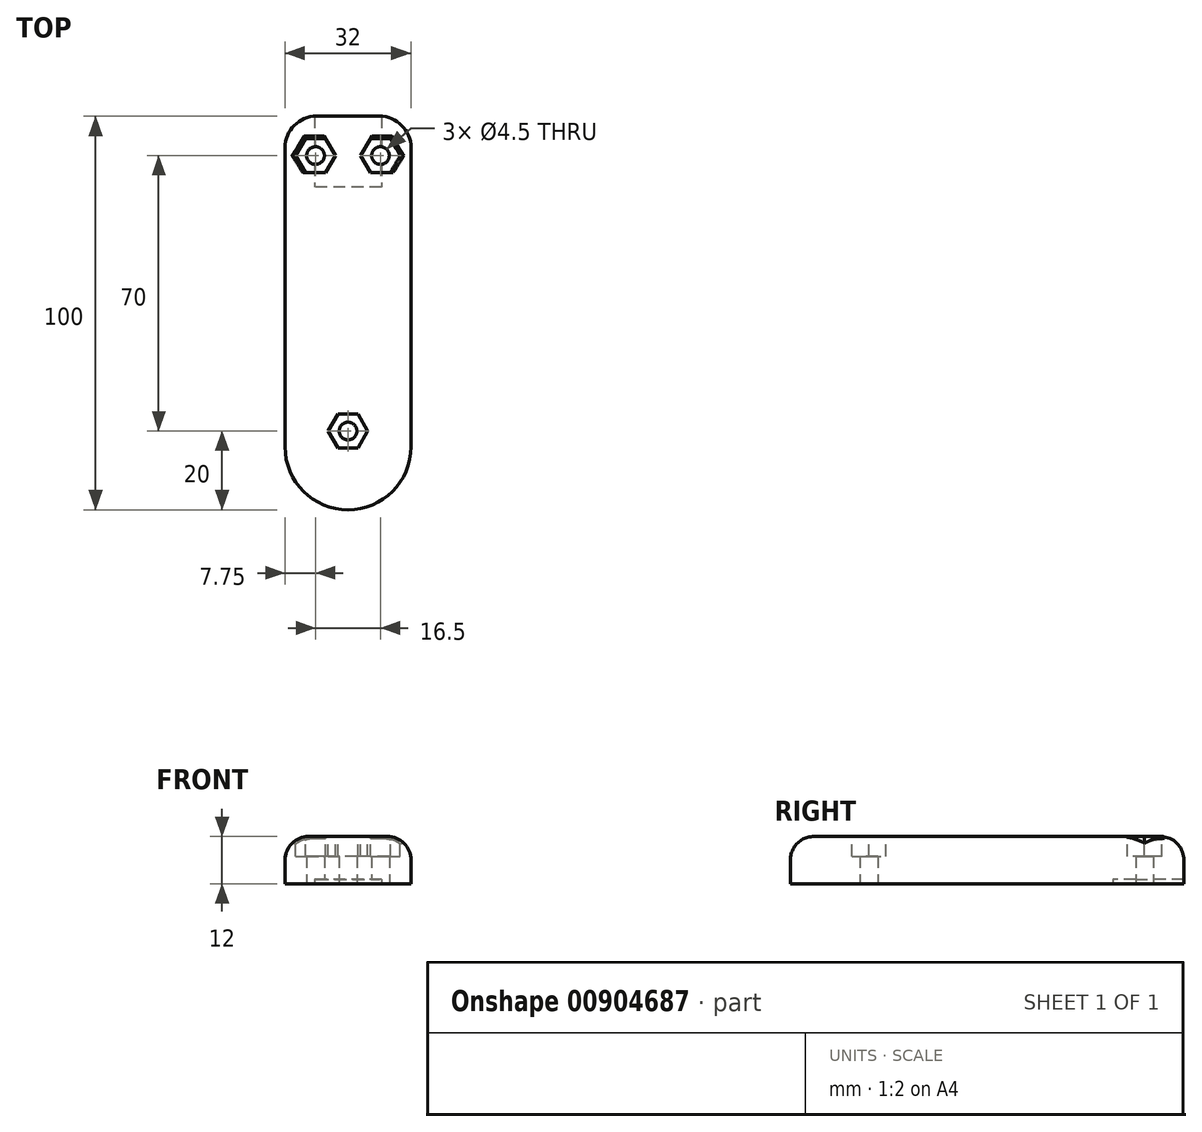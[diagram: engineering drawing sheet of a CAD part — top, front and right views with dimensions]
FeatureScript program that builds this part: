
annotation { "Feature Type Name" : "Feature", "Feature Type Description" : "" }
export const myFeature = defineFeature(function(context is Context, id is Id, definition is map)
    precondition{}
    {
        {
            var Q0;
            Q0=qCreatedBy(makeId("Top.planeOp"),FACE);
            var sketch = newSketch(context, id + "F0", { "sketchPlane" : qUnion([Q0])});
            skCircle(sketch, "E0", {"center": v(-8.25, -10) * mm, "radius": 2.25 * mm});
            skLineSegment(sketch, "E1", {"start": v(0, 0) * mm, "end": v(-8, 0) * mm});
            skLineSegment(sketch, "E2", {"start": v(-16, -8) * mm, "end": v(-16, -84) * mm});
            skLineSegment(sketch, "E3", {"start": v(0, -100) * mm, "end": v(0, -100) * mm});
            skLineSegment(sketch, "E4.MirrorCS", {"start": v(0, 0) * mm, "end": v(8, 0) * mm});
            skLineSegment(sketch, "E5.MirrorCS", {"start": v(16, -8) * mm, "end": v(16, -84) * mm});
            skCircle(sketch, "E6.MirrorC", {"center": v(8.25, -10) * mm, "radius": 2.25 * mm});
            skPoint(sketch, "E7.visualSharp", {"position": v(-16, 0) * mm});
            skArc(sketch, "E7.filletArc", {"start": v(-8, 0) * mm, "mid": v(-13.66, -2.34) * mm, "end": v(-16, -8) * mm});
            skPoint(sketch, "E8.visualSharp", {"position": v(16, 0) * mm});
            skArc(sketch, "E8.filletArc", {"start": v(16, -8) * mm, "mid": v(13.66, -2.34) * mm, "end": v(8, 0) * mm});
            skPoint(sketch, "E9.visualSharp", {"position": v(16, -100) * mm});
            skArc(sketch, "E9.filletArc", {"start": v(0, -100) * mm, "mid": v(11.31, -95.31) * mm, "end": v(16, -84) * mm});
            skPoint(sketch, "E10.visualSharp", {"position": v(-16, -100) * mm});
            skArc(sketch, "E10.filletArc", {"start": v(-16, -84) * mm, "mid": v(-11.31, -95.31) * mm, "end": v(0, -100) * mm});
            skCircle(sketch, "E11", {"center": v(0, -80) * mm, "radius": 2.25 * mm});
            skSolve(sketch);
        }
        {
            var Q0;
            Q0=makeQuery(id+"F0.imprint","IMPRINT",FACE,{"disambiguationData":[TD([[makeQuery(id+"F0.imprint","IMPRINT",EDGE,{"derivedFrom":sQuery(id+"F0.wireOp",EDGE,"E0")}),-1.0]])]});
            extrude(context, id + "F1", {"entities" : qUnion([Q0]), "depth" : 12 * mm, "offsetDistance" : 25 * mm});
        }
        {
            var Q0;
            Q0=makeQuery(id+"F1.opExtrude","CAP_FACE",FACE,{"disambiguationData":[OSD([sQuery(id+"F0.wireOp",EDGE,"E0"),sQuery(id+"F0.wireOp",EDGE,"E1"),sQuery(id+"F0.wireOp",EDGE,"E2"),sQuery(id+"F0.wireOp",EDGE,"E3"),sQuery(id+"F0.wireOp",EDGE,"E4.MirrorCS"),sQuery(id+"F0.wireOp",EDGE,"E5.MirrorCS"),sQuery(id+"F0.wireOp",EDGE,"E6.MirrorC"),sQuery(id+"F0.wireOp",EDGE,"E3"),sQuery(id+"F0.wireOp",EDGE,"E7.filletArc"),sQuery(id+"F0.wireOp",EDGE,"E8.filletArc"),sQuery(id+"F0.wireOp",EDGE,"E9.filletArc"),sQuery(id+"F0.wireOp",EDGE,"E10.filletArc")])],"isStart":false});
            var sketch = newSketch(context, id + "F2", { "sketchPlane" : qUnion([Q0])});
            skCircle(sketch, "E12.cCircle", {"center": v(-8.25, -10) * mm, "radius": 4.35 * mm, "construction": true});
            skLineSegment(sketch, "E12.0", {"start": v(-3.23, -10) * mm, "end": v(-5.74, -14.35) * mm});
            skLineSegment(sketch, "E12.1", {"start": v(-5.74, -14.35) * mm, "end": v(-10.76, -14.35) * mm});
            skLineSegment(sketch, "E12.2", {"start": v(-10.76, -14.35) * mm, "end": v(-13.27, -10) * mm});
            skLineSegment(sketch, "E12.3", {"start": v(-13.27, -10) * mm, "end": v(-10.76, -5.65) * mm});
            skLineSegment(sketch, "E12.4", {"start": v(-10.76, -5.65) * mm, "end": v(-5.74, -5.65) * mm});
            skLineSegment(sketch, "E12.5", {"start": v(-5.74, -5.65) * mm, "end": v(-3.23, -10) * mm});
            skPoint(sketch, "E12.0.midPoint", {"position": v(-4.48, -12.17) * mm});
            skLineSegment(sketch, "E13.MirrorCS", {"start": v(10.76, -14.35) * mm, "end": v(13.27, -10) * mm});
            skLineSegment(sketch, "E14.MirrorCS", {"start": v(13.27, -10) * mm, "end": v(10.76, -5.65) * mm});
            skLineSegment(sketch, "E15.MirrorCS", {"start": v(10.76, -5.65) * mm, "end": v(5.74, -5.65) * mm});
            skCircle(sketch, "E16.MirrorC", {"center": v(8.25, -10) * mm, "radius": 4.35 * mm, "construction": true});
            skLineSegment(sketch, "E17.MirrorCS", {"start": v(5.74, -5.65) * mm, "end": v(3.23, -10) * mm});
            skLineSegment(sketch, "E18.MirrorCS", {"start": v(3.23, -10) * mm, "end": v(5.74, -14.35) * mm});
            skLineSegment(sketch, "E19.MirrorCS", {"start": v(5.74, -14.35) * mm, "end": v(10.76, -14.35) * mm});
            skCircle(sketch, "E20.cCircle", {"center": v(0, -80) * mm, "radius": 4.35 * mm, "construction": true});
            skLineSegment(sketch, "E20.0", {"start": v(-5.02, -80) * mm, "end": v(-2.51, -75.65) * mm});
            skLineSegment(sketch, "E20.1", {"start": v(-2.51, -75.65) * mm, "end": v(2.51, -75.65) * mm});
            skLineSegment(sketch, "E20.2", {"start": v(2.51, -75.65) * mm, "end": v(5.02, -80) * mm});
            skLineSegment(sketch, "E20.3", {"start": v(5.02, -80) * mm, "end": v(2.51, -84.35) * mm});
            skLineSegment(sketch, "E20.4", {"start": v(2.51, -84.35) * mm, "end": v(-2.51, -84.35) * mm});
            skLineSegment(sketch, "E20.5", {"start": v(-2.51, -84.35) * mm, "end": v(-5.02, -80) * mm});
            skPoint(sketch, "E20.0.midPoint", {"position": v(-3.77, -77.83) * mm});
            skSolve(sketch);
        }
        {
            var Q0;
            Q0=makeQuery(id+"F2.imprint","IMPRINT",FACE,{"disambiguationData":[TD([[makeQuery(id+"F2.imprint","IMPRINT",EDGE,{"derivedFrom":sQuery(id+"F2.wireOp",EDGE,"E12.0")}),-1.0]])]});
            var Q1;
            Q1=makeQuery(id+"F2.imprint","IMPRINT",FACE,{"disambiguationData":[TD([[makeQuery(id+"F2.imprint","IMPRINT",EDGE,{"derivedFrom":sQuery(id+"F2.wireOp",EDGE,"E13.MirrorCS")}),1.0]])]});
            var Q2;
            Q2=makeQuery(id+"F2.imprint","IMPRINT",FACE,{"disambiguationData":[TD([[makeQuery(id+"F2.imprint","IMPRINT",EDGE,{"derivedFrom":sQuery(id+"F2.wireOp",EDGE,"E20.0")}),-1.0]])]});
            extrude(context, id + "F3", {"entities" : qUnion([Q0, Q1, Q2]), "operationType" : NewBodyOperationType.REMOVE, "oppositeDirection" : true, "depth" : 5 * mm, "offsetDistance" : 25 * mm});
        }
        {
            var Q0;
            Q0=makeQuery(id+"F1.opExtrude","CAP_EDGE",EDGE,{"disambiguationData":[OSD([sQuery(id+"F0.wireOp",EDGE,"E2")])],"isStart":false});
            fillet(context, id + "F4", {"entities" : qUnion([Q0]), "radius" : 6 * mm, "tangentPropagation" : true, "allowEdgeOverflow" : false});
        }
        {
            var Q0;
            Q0=makeQuery(id+"F1.opExtrude","CAP_FACE",FACE,{"disambiguationData":[OSD([sQuery(id+"F0.wireOp",EDGE,"E0"),sQuery(id+"F0.wireOp",EDGE,"E1"),sQuery(id+"F0.wireOp",EDGE,"E2"),sQuery(id+"F0.wireOp",EDGE,"E3"),sQuery(id+"F0.wireOp",EDGE,"E4.MirrorCS"),sQuery(id+"F0.wireOp",EDGE,"E5.MirrorCS"),sQuery(id+"F0.wireOp",EDGE,"E6.MirrorC"),sQuery(id+"F0.wireOp",EDGE,"E3"),sQuery(id+"F0.wireOp",EDGE,"E7.filletArc"),sQuery(id+"F0.wireOp",EDGE,"E8.filletArc"),sQuery(id+"F0.wireOp",EDGE,"E9.filletArc"),sQuery(id+"F0.wireOp",EDGE,"E10.filletArc")])],"isStart":true});
            var sketch = newSketch(context, id + "F5", { "sketchPlane" : qUnion([Q0])});
            skLineSegment(sketch, "E21", {"start": v(-8.5, 0) * mm, "end": v(-8.5, 18) * mm});
            skLineSegment(sketch, "E22", {"start": v(-8.5, 18) * mm, "end": v(0, 18) * mm});
            skLineSegment(sketch, "E23.MirrorCS", {"start": v(8.5, 18) * mm, "end": v(0, 18) * mm});
            skLineSegment(sketch, "E24.MirrorCS", {"start": v(8.5, 0) * mm, "end": v(8.5, 18) * mm});
            skSolve(sketch);
        }
        {
            var Q0;
            {var subQ1=sQuery(id+"F5.wireOp",EDGE,"E21");Q0=makeQuery(id+"F5.imprint","IMPRINT",FACE,{"disambiguationData":[TD([[makeQuery(id+"F5.imprint","IMPRINT",EDGE,{"derivedFrom":subQ1}),-1.0]])]});}
            extrude(context, id + "F6", {"entities" : qUnion([Q0]), "operationType" : NewBodyOperationType.REMOVE, "oppositeDirection" : true, "depth" : 1.1 * mm, "offsetDistance" : 25 * mm});
        }
        {
            var Q0;
            Q0=makeQuery(id+"F3.boolean.opBoolean","COPY",EDGE,{"derivedFrom":makeQuery(id+"F3.opExtrude","CAP_EDGE",EDGE,{"disambiguationData":[OSD([sQuery(id+"F2.wireOp",EDGE,"E12.5")])],"isStart":true})});
            var Q1;
            Q1=makeQuery(id+"F4.opFillet","BLEND_EDGE",EDGE,{"blendedFrom":[makeQuery(id+"F1.opExtrude","CAP_EDGE",EDGE,{"disambiguationData":[OSD([sQuery(id+"F0.wireOp",EDGE,"E1"),sQuery(id+"F0.wireOp",EDGE,"E4.MirrorCS")])],"isStart":false}),makeQuery(id+"F3.boolean.opBoolean","COPY",FACE,{"derivedFrom":makeQuery(id+"F3.opExtrude","SWEPT_FACE",FACE,{"disambiguationData":[OSD([sQuery(id+"F2.wireOp",EDGE,"E12.4")])]})})],"blendedInto":[makeQuery(id+"F3.boolean.opBoolean","COPY",FACE,{"derivedFrom":makeQuery(id+"F3.opExtrude","SWEPT_FACE",FACE,{"disambiguationData":[OSD([sQuery(id+"F2.wireOp",EDGE,"E12.4")])]})})]});
            var Q2;
            Q2=makeQuery(id+"F4.opFillet","BLEND_EDGE",EDGE,{"disambiguationData":[OD(1.0)],"blendedFrom":[makeQuery(id+"F1.opExtrude","CAP_EDGE",EDGE,{"disambiguationData":[OSD([sQuery(id+"F0.wireOp",EDGE,"E2")])],"isStart":false}),makeQuery(id+"F3.boolean.opBoolean","COPY",FACE,{"derivedFrom":makeQuery(id+"F3.opExtrude","SWEPT_FACE",FACE,{"disambiguationData":[OSD([sQuery(id+"F2.wireOp",EDGE,"E12.3")])]})})],"blendedInto":[makeQuery(id+"F3.boolean.opBoolean","COPY",FACE,{"derivedFrom":makeQuery(id+"F3.opExtrude","SWEPT_FACE",FACE,{"disambiguationData":[OSD([sQuery(id+"F2.wireOp",EDGE,"E12.3")])]})})]});
            var Q3;
            Q3=makeQuery(id+"F4.opFillet","BLEND_EDGE",EDGE,{"blendedFrom":[makeQuery(id+"F1.opExtrude","CAP_EDGE",EDGE,{"disambiguationData":[OSD([sQuery(id+"F0.wireOp",EDGE,"E2")])],"isStart":false}),makeQuery(id+"F3.boolean.opBoolean","COPY",FACE,{"derivedFrom":makeQuery(id+"F3.opExtrude","SWEPT_FACE",FACE,{"disambiguationData":[OSD([sQuery(id+"F2.wireOp",EDGE,"E12.2")])]})})],"blendedInto":[makeQuery(id+"F3.boolean.opBoolean","COPY",FACE,{"derivedFrom":makeQuery(id+"F3.opExtrude","SWEPT_FACE",FACE,{"disambiguationData":[OSD([sQuery(id+"F2.wireOp",EDGE,"E12.2")])]})})]});
            var Q4;
            Q4=makeQuery(id+"F3.boolean.opBoolean","COPY",EDGE,{"derivedFrom":makeQuery(id+"F3.opExtrude","CAP_EDGE",EDGE,{"disambiguationData":[OSD([sQuery(id+"F2.wireOp",EDGE,"E12.1")])],"isStart":true})});
            var Q5;
            Q5=makeQuery(id+"F3.boolean.opBoolean","COPY",EDGE,{"derivedFrom":makeQuery(id+"F3.opExtrude","CAP_EDGE",EDGE,{"disambiguationData":[OSD([sQuery(id+"F2.wireOp",EDGE,"E12.0")])],"isStart":true})});
            var Q6;
            Q6=makeQuery(id+"F3.boolean.opBoolean","COPY",EDGE,{"derivedFrom":makeQuery(id+"F3.opExtrude","CAP_EDGE",EDGE,{"disambiguationData":[OSD([sQuery(id+"F2.wireOp",EDGE,"E17.MirrorCS")])],"isStart":true})});
            var Q7;
            Q7=makeQuery(id+"F4.opFillet","BLEND_EDGE",EDGE,{"disambiguationData":[OD(1.0)],"blendedFrom":[makeQuery(id+"F1.opExtrude","CAP_EDGE",EDGE,{"disambiguationData":[OSD([sQuery(id+"F0.wireOp",EDGE,"E1"),sQuery(id+"F0.wireOp",EDGE,"E4.MirrorCS")])],"isStart":false}),makeQuery(id+"F3.boolean.opBoolean","COPY",FACE,{"derivedFrom":makeQuery(id+"F3.opExtrude","SWEPT_FACE",FACE,{"disambiguationData":[OSD([sQuery(id+"F2.wireOp",EDGE,"E15.MirrorCS")])]})})],"blendedInto":[makeQuery(id+"F3.boolean.opBoolean","COPY",FACE,{"derivedFrom":makeQuery(id+"F3.opExtrude","SWEPT_FACE",FACE,{"disambiguationData":[OSD([sQuery(id+"F2.wireOp",EDGE,"E15.MirrorCS")])]})})]});
            var Q8;
            Q8=makeQuery(id+"F4.opFillet","BLEND_EDGE",EDGE,{"blendedFrom":[makeQuery(id+"F1.opExtrude","CAP_EDGE",EDGE,{"disambiguationData":[OSD([sQuery(id+"F0.wireOp",EDGE,"E1"),sQuery(id+"F0.wireOp",EDGE,"E4.MirrorCS")])],"isStart":false}),makeQuery(id+"F3.boolean.opBoolean","COPY",FACE,{"derivedFrom":makeQuery(id+"F3.opExtrude","SWEPT_FACE",FACE,{"disambiguationData":[OSD([sQuery(id+"F2.wireOp",EDGE,"E14.MirrorCS")])]})})],"blendedInto":[makeQuery(id+"F3.boolean.opBoolean","COPY",FACE,{"derivedFrom":makeQuery(id+"F3.opExtrude","SWEPT_FACE",FACE,{"disambiguationData":[OSD([sQuery(id+"F2.wireOp",EDGE,"E14.MirrorCS")])]})})]});
            var Q9;
            Q9=makeQuery(id+"F4.opFillet","BLEND_EDGE",EDGE,{"blendedFrom":[makeQuery(id+"F1.opExtrude","CAP_EDGE",EDGE,{"disambiguationData":[OSD([sQuery(id+"F0.wireOp",EDGE,"E5.MirrorCS")])],"isStart":false}),makeQuery(id+"F3.boolean.opBoolean","COPY",FACE,{"derivedFrom":makeQuery(id+"F3.opExtrude","SWEPT_FACE",FACE,{"disambiguationData":[OSD([sQuery(id+"F2.wireOp",EDGE,"E13.MirrorCS")])]})})],"blendedInto":[makeQuery(id+"F3.boolean.opBoolean","COPY",FACE,{"derivedFrom":makeQuery(id+"F3.opExtrude","SWEPT_FACE",FACE,{"disambiguationData":[OSD([sQuery(id+"F2.wireOp",EDGE,"E13.MirrorCS")])]})})]});
            var Q10;
            Q10=makeQuery(id+"F3.boolean.opBoolean","COPY",EDGE,{"derivedFrom":makeQuery(id+"F3.opExtrude","CAP_EDGE",EDGE,{"disambiguationData":[OSD([sQuery(id+"F2.wireOp",EDGE,"E19.MirrorCS")])],"isStart":true})});
            var Q11;
            Q11=makeQuery(id+"F3.boolean.opBoolean","COPY",EDGE,{"derivedFrom":makeQuery(id+"F3.opExtrude","CAP_EDGE",EDGE,{"disambiguationData":[OSD([sQuery(id+"F2.wireOp",EDGE,"E18.MirrorCS")])],"isStart":true})});
            var Q12;
            Q12=makeQuery(id+"F3.boolean.opBoolean","COPY",EDGE,{"derivedFrom":makeQuery(id+"F3.opExtrude","CAP_EDGE",EDGE,{"disambiguationData":[OSD([sQuery(id+"F2.wireOp",EDGE,"E20.4")])],"isStart":true})});
            var Q13;
            Q13=makeQuery(id+"F3.boolean.opBoolean","COPY",EDGE,{"derivedFrom":makeQuery(id+"F3.opExtrude","CAP_EDGE",EDGE,{"disambiguationData":[OSD([sQuery(id+"F2.wireOp",EDGE,"E20.3")])],"isStart":true})});
            var Q14;
            Q14=makeQuery(id+"F3.boolean.opBoolean","COPY",EDGE,{"derivedFrom":makeQuery(id+"F3.opExtrude","CAP_EDGE",EDGE,{"disambiguationData":[OSD([sQuery(id+"F2.wireOp",EDGE,"E20.2")])],"isStart":true})});
            var Q15;
            Q15=makeQuery(id+"F3.boolean.opBoolean","COPY",EDGE,{"derivedFrom":makeQuery(id+"F3.opExtrude","CAP_EDGE",EDGE,{"disambiguationData":[OSD([sQuery(id+"F2.wireOp",EDGE,"E20.1")])],"isStart":true})});
            var Q16;
            Q16=makeQuery(id+"F3.boolean.opBoolean","COPY",EDGE,{"derivedFrom":makeQuery(id+"F3.opExtrude","CAP_EDGE",EDGE,{"disambiguationData":[OSD([sQuery(id+"F2.wireOp",EDGE,"E20.0")])],"isStart":true})});
            var Q17;
            Q17=makeQuery(id+"F3.boolean.opBoolean","COPY",EDGE,{"derivedFrom":makeQuery(id+"F3.opExtrude","CAP_EDGE",EDGE,{"disambiguationData":[OSD([sQuery(id+"F2.wireOp",EDGE,"E20.5")])],"isStart":true})});
            chamfer(context, id + "F7", {"entities" : qUnion([Q0, Q1, Q2, Q3, Q4, Q5, Q6, Q7, Q8, Q9, Q10, Q11, Q12, Q13, Q14, Q15, Q16, Q17]), "width" : 0.5 * mm, "tangentPropagation" : true});
        }
    });
